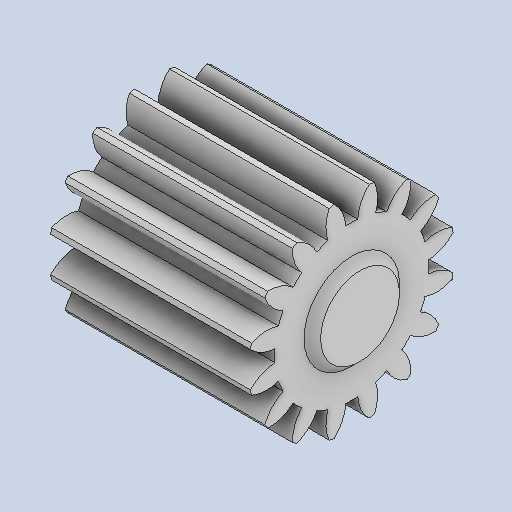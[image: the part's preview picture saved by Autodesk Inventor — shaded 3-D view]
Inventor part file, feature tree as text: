
AUTODESK INVENTOR PART (.ipt)
format: ipt  version: 2023 (Build 270158030, 158C)  size: 216,064 bytes
history: native  units: in
note: dims shown in document units (in); Inventor stores cm internally (conversion verified against a paired STEP export)
features: chamfer x1
ambient origin geometry x8: Origin, YZ Plane, XZ Plane, XY Plane, X Axis, Y Axis, Z Axis, Center Point
bodies: Solid1 (feature_tree)
feature tree (1):
  chamfer  "Chamfer1"  [1 undecoded]
note: 1 required parameter value undecoded (feature->parameter linkage not recoverable at this tier; creation-order binding heuristic only, values carry confidence <= 0.55)
